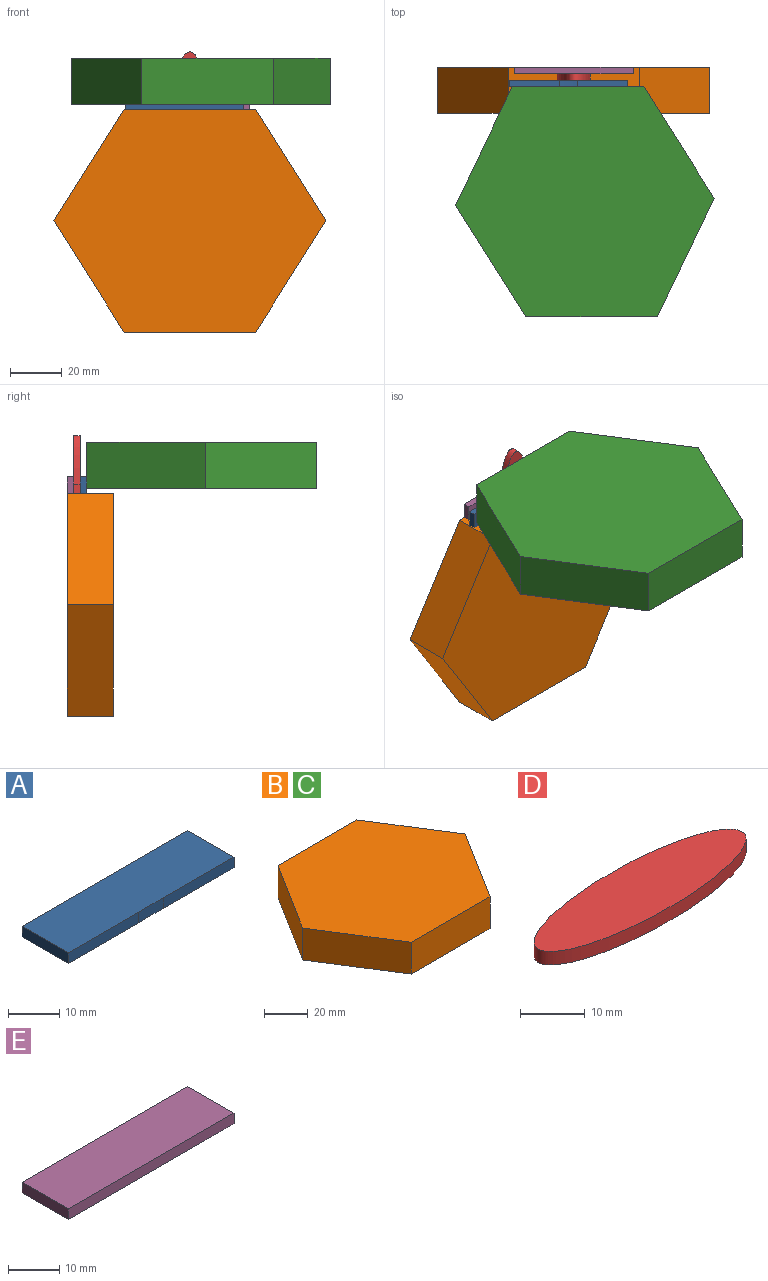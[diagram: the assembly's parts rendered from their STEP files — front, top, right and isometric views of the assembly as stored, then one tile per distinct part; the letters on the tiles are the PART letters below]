
ASSEMBLY  parts=5 mates=6
PART A: 8 faces, bbox 45.7x12.7x2.5 mm
  f0: extruded ~6.95x2.54mm, area 17.6mm2, adj f1,f5,f6,f7
  f1: plane 19.39x2.54mm, normal (0,-1,0), area 49.2mm2, adj f0,f2,f6,f7
  f2: plane 12.7x2.54mm, normal (1,0,0), area 32.3mm2, adj f1,f3,f6,f7
  f3: plane 45.72x2.54mm, normal (0,1,0), area 116.1mm2, adj f2,f4,f6,f7
  f4: plane 12.7x2.54mm, normal (-1,0,0), area 32.3mm2, adj f3,f5,f6,f7
  f5: plane 19.39x2.54mm, normal (0,-1,0), area 49.2mm2, adj f0,f4,f6,f7
  f6: plane 45.72x12.7mm, normal (0,0,1), area 580.3mm2, adj f0,f1,f2,f3,f4,f5
  f7: plane 45.72x12.7mm, normal (0,0,-1), area 580.3mm2, adj f0,f1,f2,f3,f4,f5
PART B: 8 faces, bbox 105x85.9x17.8 mm
  f0: plane 50.8x17.78mm, normal (0,1,0), area 903.2mm2, adj f1,f5,f6,f7
  f1: plane 42.97x27.09mm, normal (-0.85,0.53,0), area 903.2mm2, adj f0,f2,f6,f7
  f2: plane 42.97x27.09mm, normal (-0.85,-0.53,0), area 903.2mm2, adj f1,f3,f6,f7
  f3: plane 50.8x17.78mm, normal (0,-1,0), area 903.2mm2, adj f2,f4,f6,f7
  f4: plane 42.97x27.09mm, normal (0.85,-0.53,0), area 903.2mm2, adj f3,f5,f6,f7
  f5: plane 42.97x27.09mm, normal (0.85,0.53,0), area 903.2mm2, adj f0,f4,f6,f7
  f6: plane 104.98x85.95mm, normal (0,0,1), area 6694.5mm2, adj f0,f1,f2,f3,f4,f5
  f7: plane 104.98x85.95mm, normal (0,0,-1), area 6694.5mm2, adj f0,f1,f2,f3,f4,f5
PART C: same geometry as B
PART D: 4 faces, bbox 44.3x12.8x2.5 mm
  f0: plane 6.95x2.54mm, normal (0,1,0), area 17.6mm2, adj f1,f2,f3
  f1: extruded ~44.17x12.84mm, area 228.2mm2, adj f0,f2,f3
  f2: plane 44.3x12.84mm, normal (0,0,1), area 449.1mm2, adj f0,f1
  f3: plane 44.3x12.84mm, normal (0,0,-1), area 449.1mm2, adj f0,f1
PART E: 6 faces, bbox 45.7x12.7x2.5 mm
  f0: plane 45.72x2.54mm, normal (0,1,0), area 116.1mm2, adj f1,f3,f4,f5
  f1: plane 12.7x2.54mm, normal (-1,0,0), area 32.3mm2, adj f0,f2,f4,f5
  f2: plane 45.72x2.54mm, normal (0,-1,0), area 116.1mm2, adj f1,f3,f4,f5
  f3: plane 12.7x2.54mm, normal (1,0,0), area 32.3mm2, adj f0,f2,f4,f5
  f4: plane 45.72x12.7mm, normal (0,0,1), area 580.6mm2, adj f0,f1,f2,f3
  f5: plane 45.72x12.7mm, normal (0,0,-1), area 580.6mm2, adj f0,f1,f2,f3
PLACE A rot(axis=(0,0.71,-0.71),180deg) t=(41.53,66.64,114.94)mm
PLACE B rot(axis=(-1,0,0),90deg) t=(84.64,53.94,56.12)mm
PLACE C rot(axis=(0,0,1),122.2deg) t=(96.36,32.92,83.65)mm
PLACE D rot(axis=(-0.58,0.58,0.58),120deg) t=(100.43,66.64,45.46)mm
PLACE E rot(axis=(-1,0,0),90deg) t=(115.51,69.18,89.4)mm
MATE planar E.f5 <-> D.f2  axis (0,-1,0) through (79.95,69.18,81.73)mm
MATE planar A.f6 <-> C.f4  axis (0,-1,0) through (77.8,64.1,81.73)mm
MATE planar D.f2 <-> E.f5  axis (0,1,0) through (79.95,69.18,81.73)mm
MATE planar D.f3 <-> A.f7  axis (0,-1,0) through (79.95,66.64,81.73)mm
MATE planar B.f6 <-> E.f4  axis (0,1,0) through (79.95,71.72,81.73)mm
MATE planar E.f4 <-> B.f3  axis (0,1,0) through (79.95,71.72,81.73)mm
